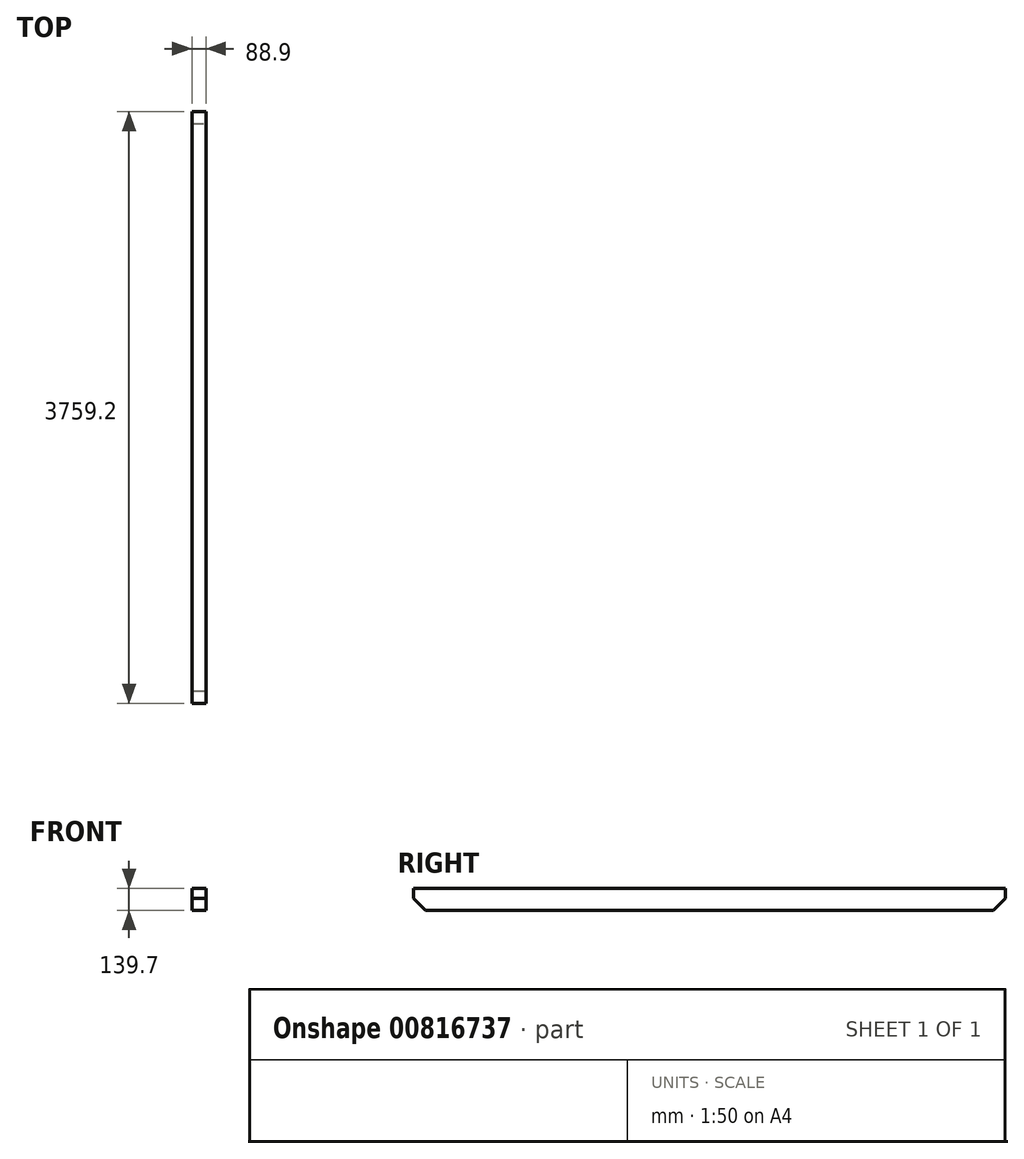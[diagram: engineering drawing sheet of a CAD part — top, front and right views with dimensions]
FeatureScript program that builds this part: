
annotation { "Feature Type Name" : "Feature", "Feature Type Description" : "" }
export const myFeature = defineFeature(function(context is Context, id is Id, definition is map)
    precondition{}
    {
        {
            var Q0;
            Q0=qCreatedBy(makeId("Front.planeOp"),FACE);
            var sketch = newSketch(context, id + "F0", { "sketchPlane" : qUnion([Q0])});
            skLineSegment(sketch, "E0.bottom", {"start": v(44.45, -69.85) * mm, "end": v(-44.45, -69.85) * mm});
            skLineSegment(sketch, "E0.top", {"start": v(44.45, 69.85) * mm, "end": v(-44.45, 69.85) * mm});
            skLineSegment(sketch, "E0.left", {"start": v(44.45, -69.85) * mm, "end": v(44.45, 69.85) * mm});
            skLineSegment(sketch, "E0.right", {"start": v(-44.45, -69.85) * mm, "end": v(-44.45, 69.85) * mm});
            skPoint(sketch, "E0.middle", {"position": v(0, 0) * mm});
            skSolve(sketch);
        }
        {
            var Q0;
            Q0 = qSketchRegion(id + "F0", true);
            extrude(context, id + "F1", {"entities" : qUnion([Q0]), "endBound" : BoundingType.SYMMETRIC, "depth" : 3759.2 * mm, "offsetDistance" : 25.4 * mm});
        }
        {
            var Q0;
            Q0=makeQuery(id+"F1.opExtrude","CAP_EDGE",EDGE,{"disambiguationData":[OSD([sQuery(id+"F0.wireOp",EDGE,"E0.bottom")])],"isStart":false});
            var Q1;
            Q1=makeQuery(id+"F1.opExtrude","CAP_EDGE",EDGE,{"disambiguationData":[OSD([sQuery(id+"F0.wireOp",EDGE,"E0.bottom")])],"isStart":true});
            chamfer(context, id + "F2", {"entities" : qUnion([Q0, Q1]), "width" : 76.2 * mm, "tangentPropagation" : true});
        }
    });
